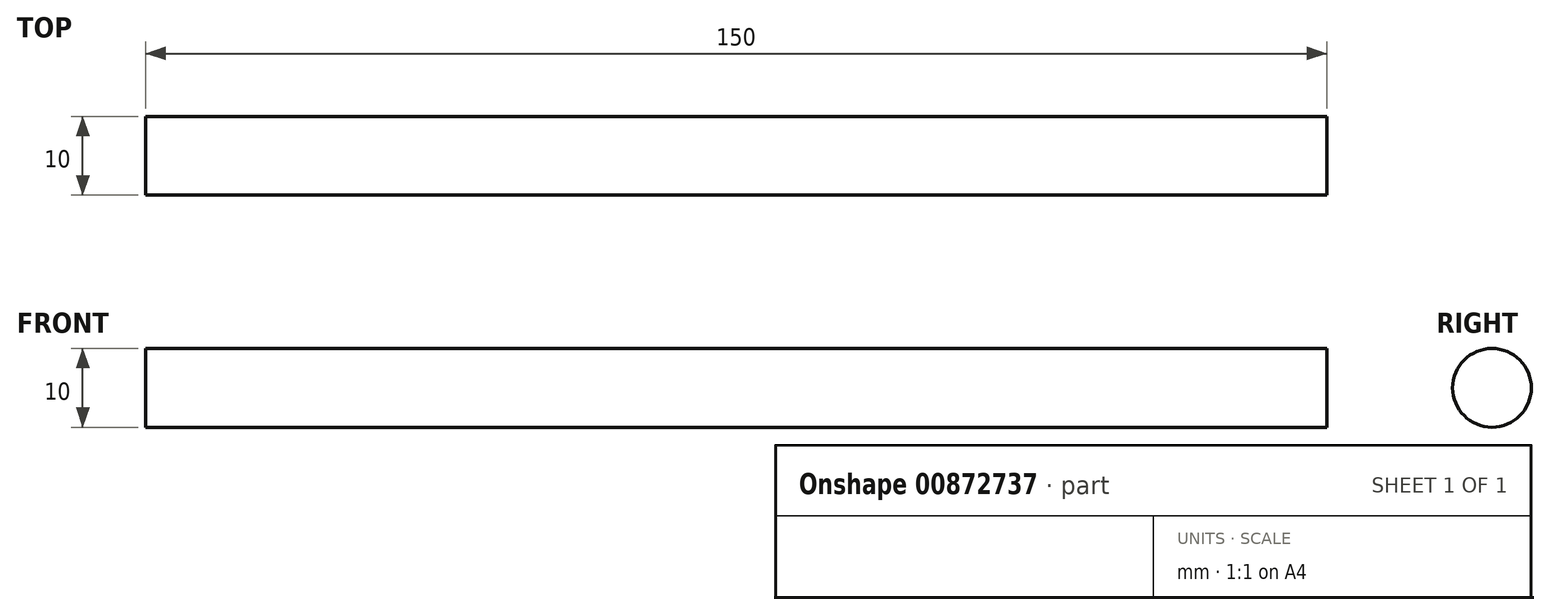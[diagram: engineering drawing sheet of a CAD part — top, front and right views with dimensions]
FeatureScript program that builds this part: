
annotation { "Feature Type Name" : "Feature", "Feature Type Description" : "" }
export const myFeature = defineFeature(function(context is Context, id is Id, definition is map)
    precondition{}
    {
        {
            var Q0;
            Q0=qCreatedBy(makeId("Front.planeOp"),FACE);
            var sketch = newSketch(context, id + "F0", { "sketchPlane" : qUnion([Q0])});
            skLineSegment(sketch, "E0.bottom", {"start": v(-75, 5) * mm, "end": v(75, 5) * mm});
            skLineSegment(sketch, "E0.top", {"start": v(-75, 0) * mm, "end": v(75, 0) * mm});
            skLineSegment(sketch, "E0.left", {"start": v(-75, 5) * mm, "end": v(-75, 0) * mm});
            skLineSegment(sketch, "E0.right", {"start": v(75, 5) * mm, "end": v(75, 0) * mm});
            skSolve(sketch);
        }
        {
            var Q0;
            Q0=makeQuery(id+"F0.imprint","IMPRINT",FACE,{"disambiguationData":[TD([[makeQuery(id+"F0.imprint","IMPRINT",EDGE,{"derivedFrom":sQuery(id+"F0.wireOp",EDGE,"E0.bottom")}),-1.0]])]});
            var Q1;
            Q1=sQuery(id+"F0.wireOp",EDGE,"E0.top");
            revolve(context, id + "F1", {"surfaceOperationType" : NewSurfaceOperationType.NEW, "entities" : qUnion([Q0]), "axis" : qUnion([Q1]), "revolveType" : RevolveType.FULL});
        }
    });
